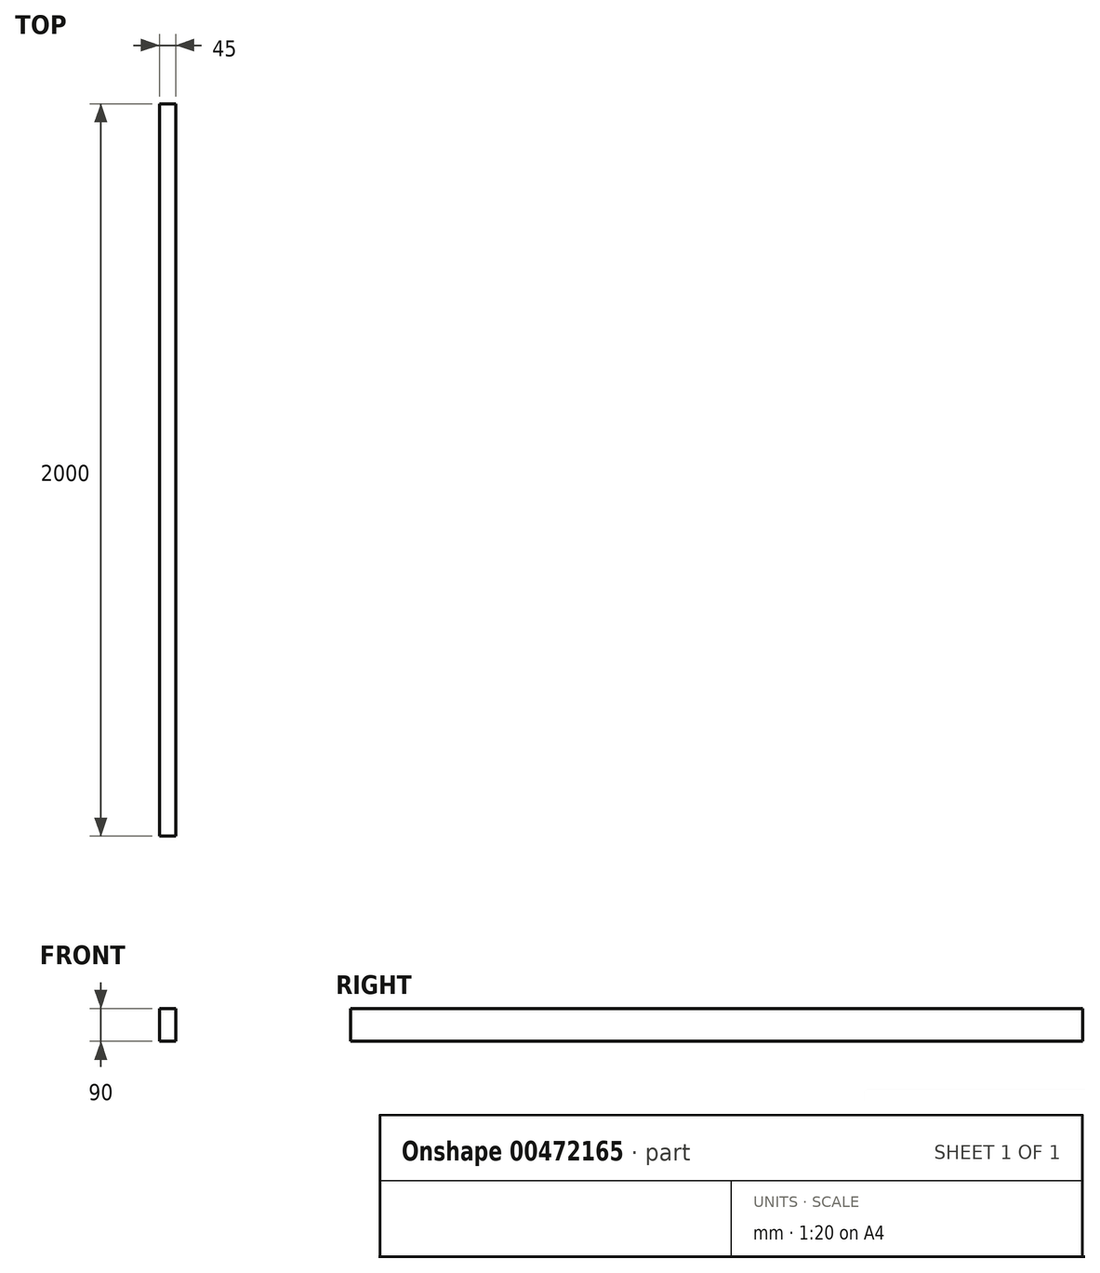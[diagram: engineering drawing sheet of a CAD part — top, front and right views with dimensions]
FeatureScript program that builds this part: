
annotation { "Feature Type Name" : "Feature", "Feature Type Description" : "" }
export const myFeature = defineFeature(function(context is Context, id is Id, definition is map)
    precondition{}
    {
        {
            var Q0;
            Q0=qCreatedBy(makeId("Front.planeOp"),FACE);
            var sketch = newSketch(context, id + "F0", { "sketchPlane" : qUnion([Q0])});
            skLineSegment(sketch, "E0.bottom", {"start": v(-22.5, 45) * mm, "end": v(22.5, 45) * mm});
            skLineSegment(sketch, "E0.top", {"start": v(-22.5, -45) * mm, "end": v(22.5, -45) * mm});
            skLineSegment(sketch, "E0.left", {"start": v(-22.5, 45) * mm, "end": v(-22.5, -45) * mm});
            skLineSegment(sketch, "E0.right", {"start": v(22.5, 45) * mm, "end": v(22.5, -45) * mm});
            skPoint(sketch, "E0.middle", {"position": v(0, 0) * mm});
            skSolve(sketch);
        }
        {
            var Q0;
            Q0 = qSketchRegion(id + "F0", true);
            extrude(context, id + "F1", {"entities" : qUnion([Q0]), "endBound" : BoundingType.SYMMETRIC, "depth" : 2000 * mm});
        }
    });
